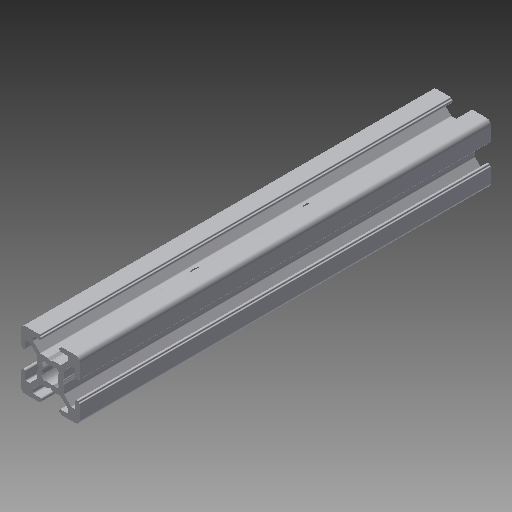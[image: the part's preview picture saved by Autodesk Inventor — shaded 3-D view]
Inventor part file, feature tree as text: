
AUTODESK INVENTOR PART (.ipt)
format: ipt  version: 2017 (Build 210142000, 142)  size: 414,720 bytes
history: native  units: in
note: dims shown in document units (in); Inventor stores cm internally (conversion verified against a paired STEP export)
features: other x3, sketch x2, extrude x1, hole x1, mirror x1
ambient origin geometry x8: Origin, YZ Plane, XZ Plane, XY Plane, X Axis, Y Axis, Z Axis, Center Point
bodies: Solid1 (feature_tree)
feature tree (8):
  other  "Blocks"
  extrude  "Extrusion1"  Depth=2.0in
  hole  "Hole1"  [1 undecoded]
  mirror  "Mirror1"
  sketch  "Sketch1"  dims[d1=0.0in d5=2.0in]
  other  "20x20"
  sketch  "Sketch3"  dims[d6=0.187in d7=0.75in d8=0.375in d9=0.25in d10=0.5635in d11=1.0in d12=0.8108in d13=1.0in d14=1.0in]
  other  "20x20:1"
note: 1 required parameter value undecoded (feature->parameter linkage not recoverable at this tier; creation-order binding heuristic only, values carry confidence <= 0.55)
